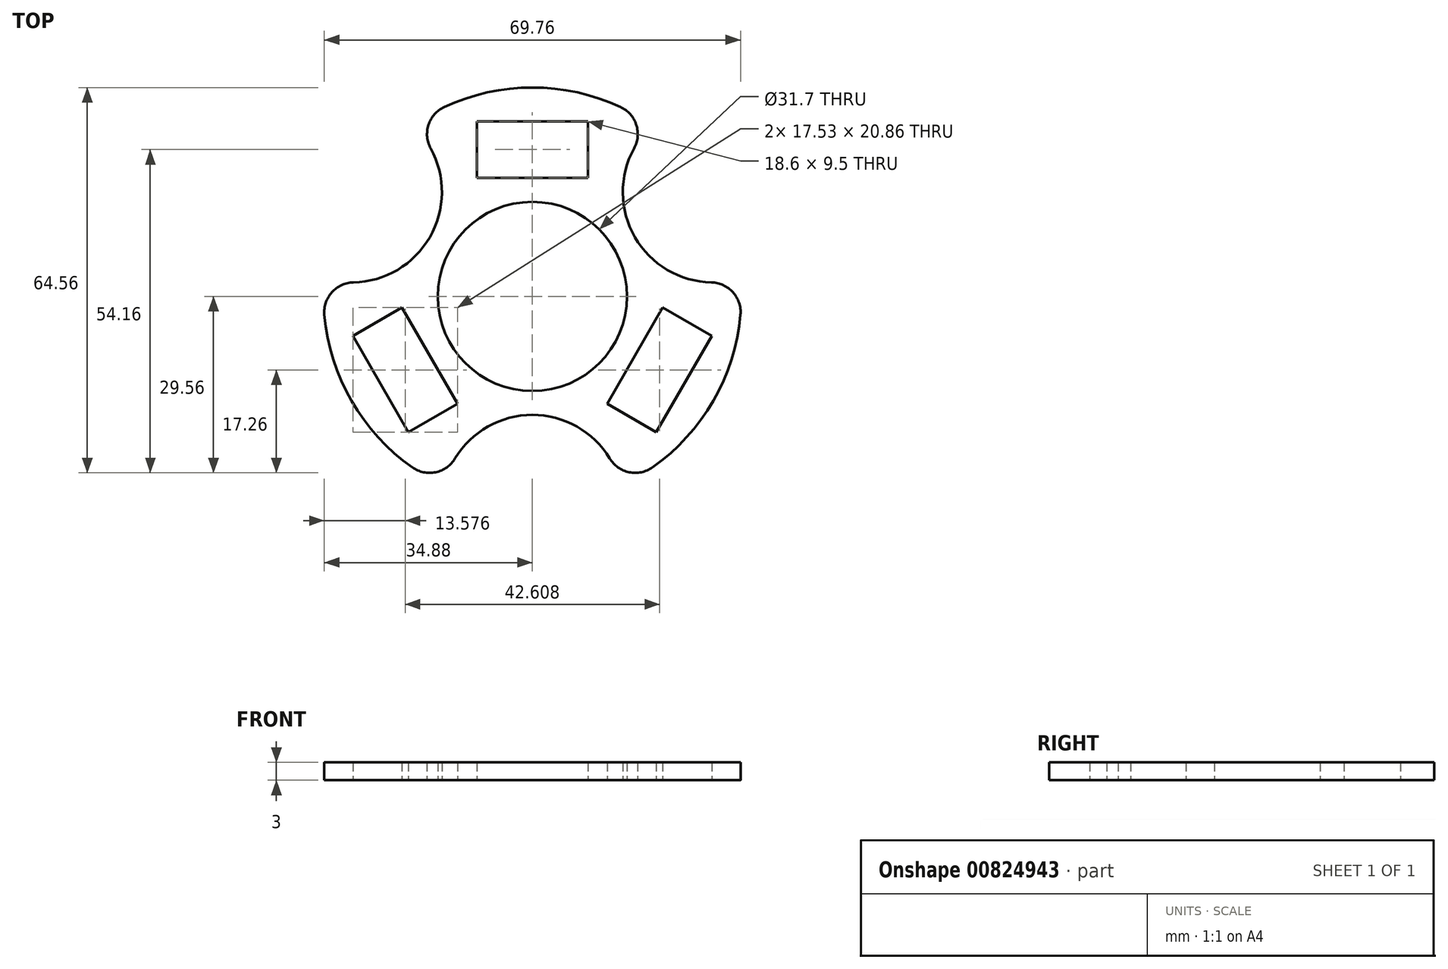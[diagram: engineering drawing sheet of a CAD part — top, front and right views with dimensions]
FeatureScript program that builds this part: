
annotation { "Feature Type Name" : "Feature", "Feature Type Description" : "" }
export const myFeature = defineFeature(function(context is Context, id is Id, definition is map)
    precondition{}
    {
        {
            var Q0;
            Q0=qCreatedBy(makeId("Top.planeOp"),FACE);
            var sketch = newSketch(context, id + "F0", { "sketchPlane" : qUnion([Q0])});
            skCircle(sketch, "E0", {"center": v(0, 0) * mm, "radius": 15.85 * mm});
            skArc(sketch, "E1", {"start": v(-34.86, -3.09) * mm, "mid": v(-30.31, -17.5) * mm, "end": v(-20.1, -28.65) * mm});
            skLineSegment(sketch, "E2.bottom", {"start": v(-9.3, 29.35) * mm, "end": v(9.3, 29.35) * mm});
            skLineSegment(sketch, "E2.top", {"start": v(-9.3, 19.85) * mm, "end": v(9.3, 19.85) * mm});
            skLineSegment(sketch, "E2.left", {"start": v(-9.3, 29.35) * mm, "end": v(-9.3, 19.85) * mm});
            skLineSegment(sketch, "E2.right", {"start": v(9.3, 29.35) * mm, "end": v(9.3, 19.85) * mm});
            skLineSegment(sketch, "E3", {"start": v(0, 19.85) * mm, "end": v(0, 15.85) * mm, "construction": true});
            skLineSegment(sketch, "E4.1.0", {"start": v(-30.07, -6.62) * mm, "end": v(-21.84, -1.87) * mm});
            skLineSegment(sketch, "E4.1.1", {"start": v(-20.77, -22.73) * mm, "end": v(-30.07, -6.62) * mm});
            skLineSegment(sketch, "E4.1.2", {"start": v(-20.77, -22.73) * mm, "end": v(-12.54, -17.98) * mm});
            skLineSegment(sketch, "E4.1.3", {"start": v(-12.54, -17.98) * mm, "end": v(-21.84, -1.87) * mm});
            skLineSegment(sketch, "E4.2.0", {"start": v(20.77, -22.73) * mm, "end": v(12.54, -17.98) * mm});
            skLineSegment(sketch, "E4.2.1", {"start": v(30.07, -6.62) * mm, "end": v(20.77, -22.73) * mm});
            skLineSegment(sketch, "E4.2.2", {"start": v(30.07, -6.62) * mm, "end": v(21.84, -1.87) * mm});
            skLineSegment(sketch, "E4.2.3", {"start": v(21.84, -1.87) * mm, "end": v(12.54, -17.98) * mm});
            skArc(sketch, "E5", {"start": v(-29.99, 2.35) * mm, "mid": v(-17.2, 9.92) * mm, "end": v(-17.03, 24.8) * mm});
            skLineSegment(sketch, "E6", {"start": v(-30.31, 17.5) * mm, "end": v(-9.3, 29.35) * mm, "construction": true});
            skLineSegment(sketch, "E7", {"start": v(-30.31, 17.5) * mm, "end": v(-30.07, -6.62) * mm, "construction": true});
            skLineSegment(sketch, "E8", {"start": v(0, 0) * mm, "end": v(-13.73, 7.92) * mm, "construction": true});
            skLineSegment(sketch, "E9", {"start": v(-13.73, 7.92) * mm, "end": v(-17.2, 9.93) * mm, "construction": true});
            skLineSegment(sketch, "E10", {"start": v(-17.2, 9.92) * mm, "end": v(-30.31, 17.5) * mm, "construction": true});
            skArc(sketch, "E11.1.0", {"start": v(12.96, -27.15) * mm, "mid": v(0, -19.85) * mm, "end": v(-12.96, -27.15) * mm});
            skArc(sketch, "E11.2.0", {"start": v(17.03, 24.8) * mm, "mid": v(17.2, 9.93) * mm, "end": v(29.99, 2.35) * mm});
            skArc(sketch, "E12.trimOffspring", {"start": v(14.76, 31.74) * mm, "mid": v(0, 35) * mm, "end": v(-14.76, 31.74) * mm});
            skArc(sketch, "E13.trimOffspring", {"start": v(20.1, -28.65) * mm, "mid": v(30.31, -17.5) * mm, "end": v(34.86, -3.09) * mm});
            skPoint(sketch, "E14.visualSharp", {"position": v(-20.08, 28.67) * mm});
            skArc(sketch, "E14.filletArc", {"start": v(-14.76, 31.74) * mm, "mid": v(-17.4, 28.76) * mm, "end": v(-17.03, 24.8) * mm});
            skPoint(sketch, "E15.visualSharp", {"position": v(20.08, 28.67) * mm});
            skArc(sketch, "E15.filletArc", {"start": v(17.03, 24.8) * mm, "mid": v(17.4, 28.76) * mm, "end": v(14.76, 31.74) * mm});
            skPoint(sketch, "E16.visualSharp", {"position": v(34.87, 3.05) * mm});
            skArc(sketch, "E16.filletArc", {"start": v(34.86, -3.09) * mm, "mid": v(33.6, 0.7) * mm, "end": v(29.99, 2.35) * mm});
            skPoint(sketch, "E17.visualSharp", {"position": v(14.8, -31.72) * mm});
            skArc(sketch, "E17.filletArc", {"start": v(12.96, -27.15) * mm, "mid": v(16.2, -29.45) * mm, "end": v(20.1, -28.65) * mm});
            skPoint(sketch, "E18.visualSharp", {"position": v(-14.8, -31.72) * mm});
            skArc(sketch, "E18.filletArc", {"start": v(-20.1, -28.65) * mm, "mid": v(-16.2, -29.45) * mm, "end": v(-12.96, -27.15) * mm});
            skPoint(sketch, "E19.visualSharp", {"position": v(-34.87, 3.05) * mm});
            skArc(sketch, "E19.filletArc", {"start": v(-29.99, 2.35) * mm, "mid": v(-33.6, 0.7) * mm, "end": v(-34.86, -3.09) * mm});
            skSolve(sketch);
        }
        {
            var Q0;
            Q0=makeQuery(id+"F0.imprint","IMPRINT",FACE,{"disambiguationData":[TD([[makeQuery(id+"F0.imprint","IMPRINT",EDGE,{"derivedFrom":sQuery(id+"F0.wireOp",EDGE,"E0")}),-1.0]])]});
            extrude(context, id + "F1", {"entities" : qUnion([Q0]), "endBound" : BoundingType.SYMMETRIC, "depth" : 3 * mm, "offsetDistance" : 25 * mm});
        }
    });
